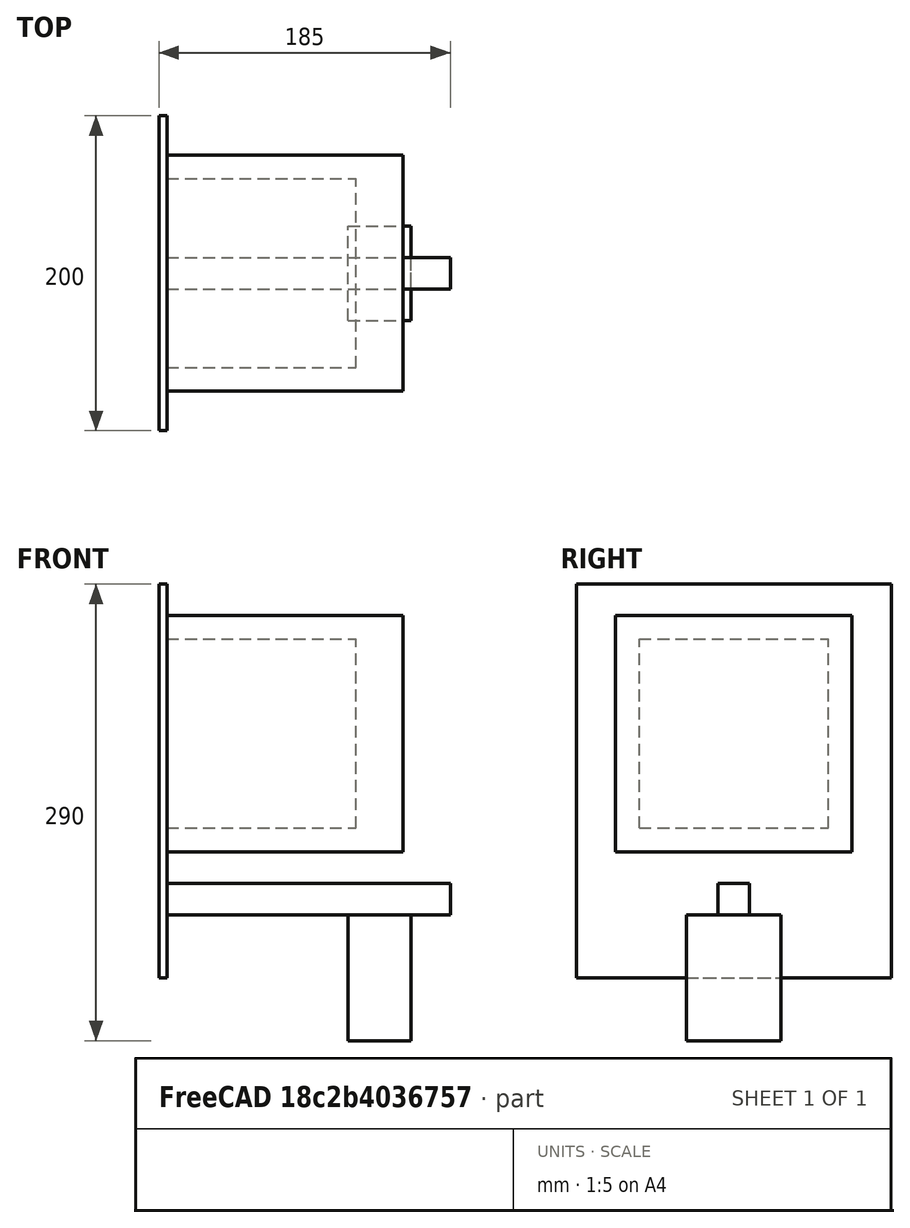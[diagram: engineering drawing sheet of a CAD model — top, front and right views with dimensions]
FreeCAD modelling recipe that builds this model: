
FCSTD DOCUMENT  (FreeCAD 0.17R13541 (Git))
Label: centralNode
License: All rights reserved
LicenseURL: http://en.wikipedia.org/wiki/All_rights_reserved
objects: Part::Box×5, Mesh::Feature×5, App::DocumentObjectGroup×1
note: 5 computed .brp shape members not serialized (recipe doc carries the construction recipe); baked Part::Feature solids carry a one-line shape summary decoded from their .brp

FEATURE [Part::Box] Box  label="Housing"
  AttacherType = Attacher::AttachEngine3D
  Height = 150
  Length = 150
  Placement = pos=(5,25,80) rot=(0,0,1;0rad)
  Width = 150
FEATURE [Part::Box] Box001  label="Base"
  AttacherType = Attacher::AttachEngine3D
  Height = 250
  Length = 5
  Width = 200
FEATURE [Part::Box] Box002  label="Support"
  AttacherType = Attacher::AttachEngine3D
  Height = 20
  Length = 180
  Placement = pos=(5,90,40) rot=(0,0,1;0rad)
  Width = 20
FEATURE [Mesh::Feature] Solid_Plate  label="TopPlate"
  Placement = pos=(126,100,107) rot=(0.707107,0.707107,0;3.14159rad)
FEATURE [Mesh::Feature] Middle_Ring  label="MiddlePlate1"
  Placement = pos=(127,100,87) rot=(-0.707107,-0.707107,0;3.14159rad)
FEATURE [Mesh::Feature] Middle_Ring001  label="MiddlePlate2"
  Placement = pos=(127,100,67) rot=(-0.707107,-0.707107,0;3.14159rad)
FEATURE [Mesh::Feature] Middle_Ring002  label="MiddlePlate3"
  Placement = pos=(127,100,47) rot=(-0.707107,-0.707107,0;3.14159rad)
FEATURE [Mesh::Feature] Solid_Plate001  label="BottomPlate"
  Placement = pos=(126,100,27) rot=(0.707107,0.707107,0;3.14159rad)
FEATURE [Part::Box] Box003  label="Sensors"
  AttacherType = Attacher::AttachEngine3D
  Height = 80
  Length = 40
  Placement = pos=(120,70,-40) rot=(0,0,1;0rad)
  Width = 60
FEATURE [Part::Box] Box004  label="Circuits"
  AttacherType = Attacher::AttachEngine3D
  Height = 120
  Length = 120
  Placement = pos=(5,40,95) rot=(0,0,1;0rad)
  Width = 120
FEATURE [App::DocumentObjectGroup] Group  label="nodeHousing"
  Group = -> [Box,Box001,Box002,Solid_Plate,Middle_Ring,Middle_Ring001,Middle_Ring002,Solid_Plate001,Box003,Box004]
